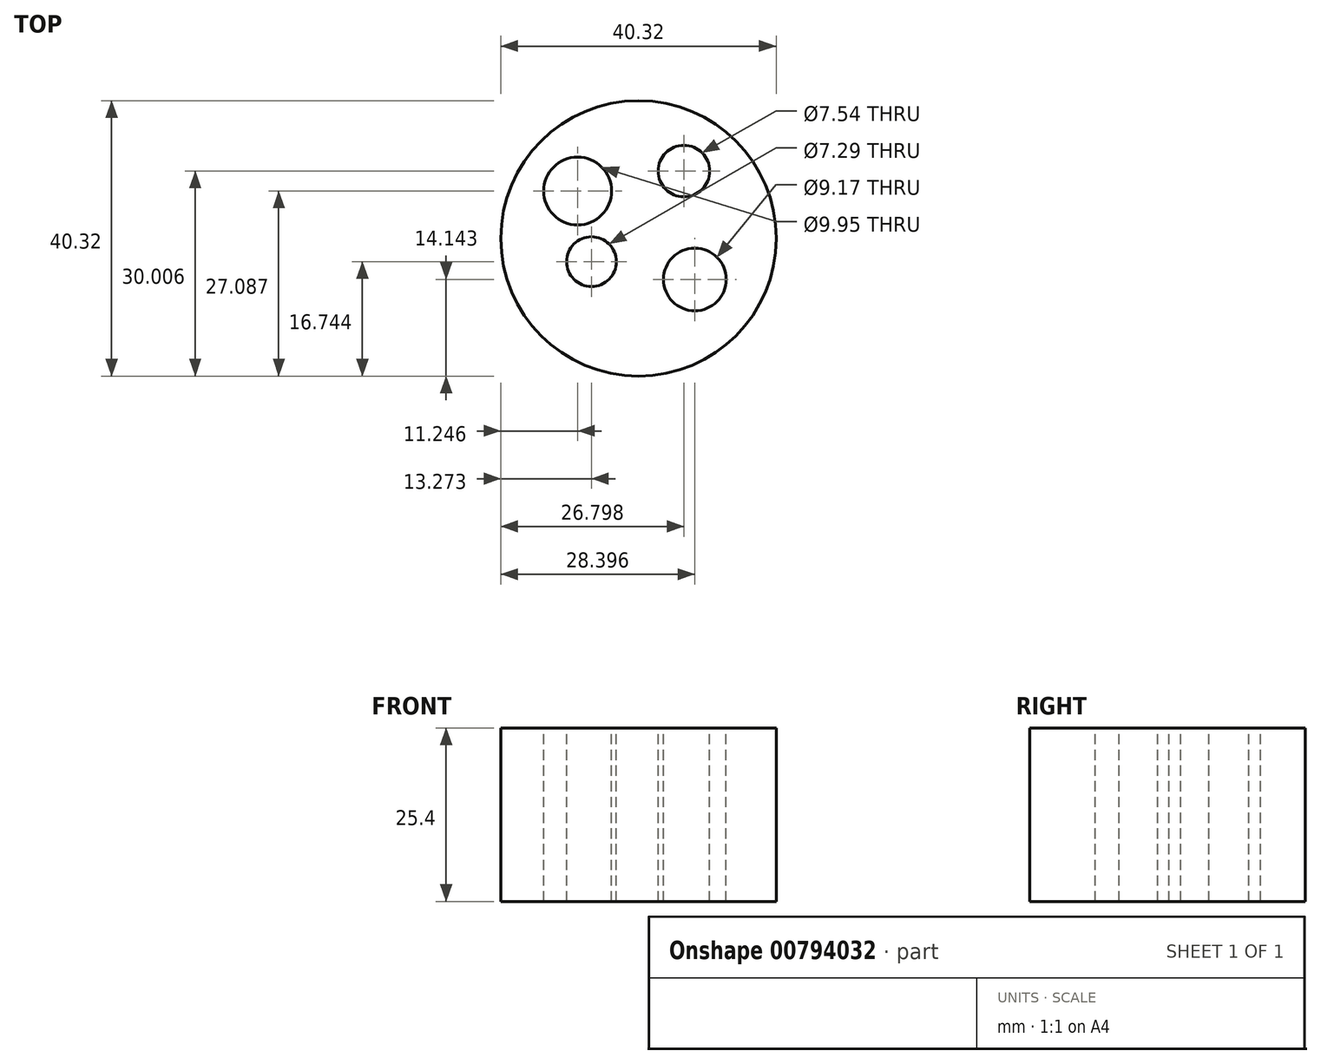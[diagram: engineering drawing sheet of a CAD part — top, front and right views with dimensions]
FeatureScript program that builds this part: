
annotation { "Feature Type Name" : "Feature", "Feature Type Description" : "" }
export const myFeature = defineFeature(function(context is Context, id is Id, definition is map)
    precondition{}
    {
        {
            var Q0;
            Q0=qCreatedBy(makeId("Top.planeOp"),FACE);
            var sketch = newSketch(context, id + "F0", { "sketchPlane" : qUnion([Q0])});
            skCircle(sketch, "E0", {"center": v(0, 0) * mm, "radius": 20.16 * mm});
            skSolve(sketch);
        }
        {
            var Q0;
            Q0 = qSketchRegion(id + "F0", true);
            extrude(context, id + "F1", {"entities" : qUnion([Q0]), "depth" : 25.4 * mm, "offsetDistance" : 25.4 * mm});
        }
        {
            var Q0;
            Q0=makeQuery(id+"F1.opExtrude","CAP_FACE",FACE,{"disambiguationData":[OSD([sQuery(id+"F0.wireOp",EDGE,"E0")])],"isStart":false});
            var sketch = newSketch(context, id + "F2", { "sketchPlane" : qUnion([Q0])});
            skCircle(sketch, "E1", {"center": v(6.64, 9.85) * mm, "radius": 3.77 * mm});
            skCircle(sketch, "E2", {"center": v(-8.91, 6.93) * mm, "radius": 4.98 * mm});
            skCircle(sketch, "E3", {"center": v(8.24, -6.02) * mm, "radius": 4.59 * mm});
            skCircle(sketch, "E4", {"center": v(-6.89, -3.42) * mm, "radius": 3.65 * mm});
            skSolve(sketch);
        }
        {
            var Q0;
            Q0 = qSketchRegion(id + "F2", true);
            extrude(context, id + "F3", {"entities" : qUnion([Q0]), "operationType" : NewBodyOperationType.REMOVE, "oppositeDirection" : true, "depth" : 25.4 * mm, "offsetDistance" : 25.4 * mm});
        }
    });
